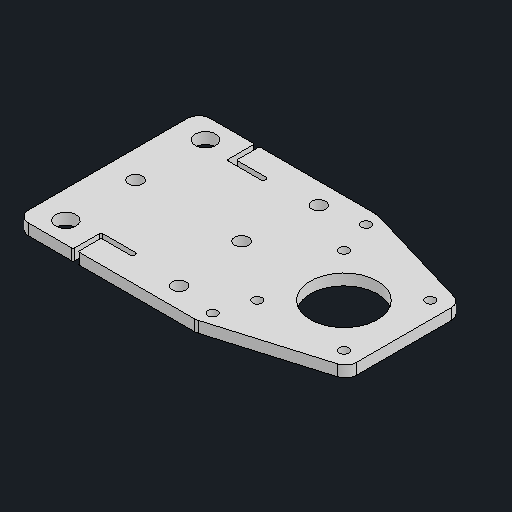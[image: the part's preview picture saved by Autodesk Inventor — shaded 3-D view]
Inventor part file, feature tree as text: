
AUTODESK INVENTOR PART (.ipt)
format: ipt  version: 2024.2 (Build 282272000, 272)  size: 118,784 bytes
history: native  units: mm
features: other x1, fillet x1
ambient origin geometry x8: Origin, YZ Plane, XZ Plane, XY Plane, X Axis, Y Axis, Z Axis, Center Point
bodies: Body1 (feature_tree)
feature tree (2):
  other  "솔리드1"
  fillet  "Fillet2"  [1 undecoded]
note: 1 required parameter value undecoded (feature->parameter linkage not recoverable at this tier; creation-order binding heuristic only, values carry confidence <= 0.55)
